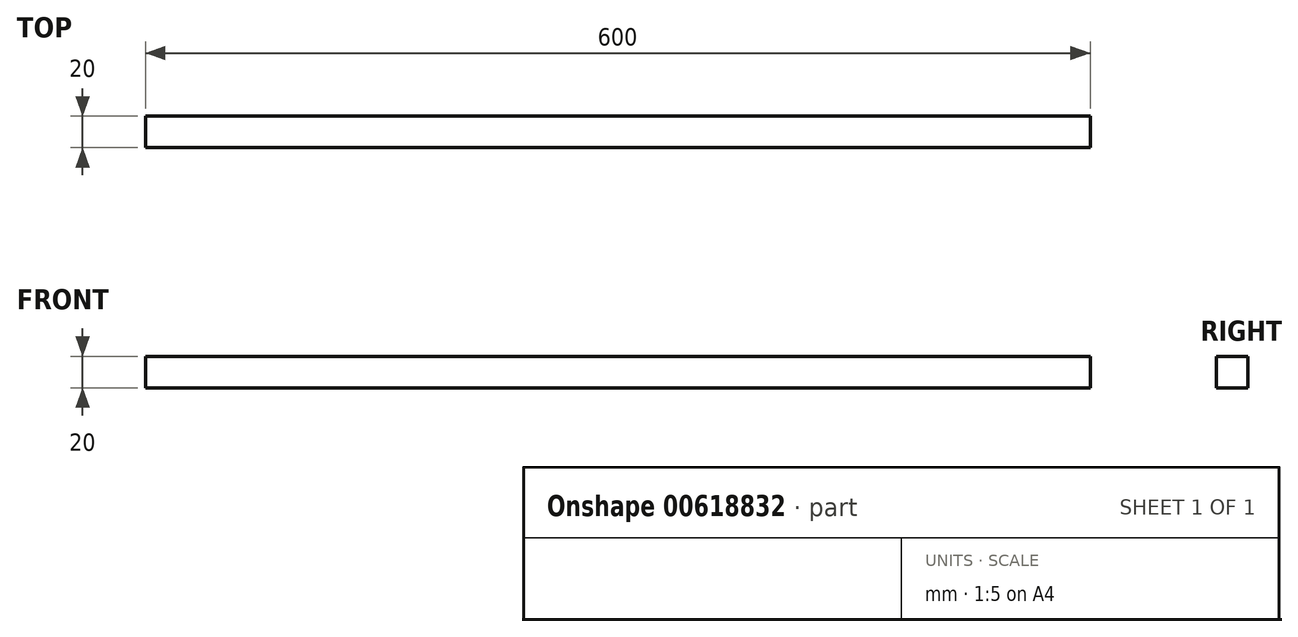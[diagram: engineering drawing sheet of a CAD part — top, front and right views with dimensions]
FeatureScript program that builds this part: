
annotation { "Feature Type Name" : "Feature", "Feature Type Description" : "" }
export const myFeature = defineFeature(function(context is Context, id is Id, definition is map)
    precondition{}
    {
        {
            var Q0;
            Q0=qCreatedBy(makeId("Top.planeOp"),FACE);
            var sketch = newSketch(context, id + "F0", { "sketchPlane" : qUnion([Q0])});
            skLineSegment(sketch, "E0.bottom", {"start": v(-300, 10) * mm, "end": v(300, 10) * mm});
            skLineSegment(sketch, "E0.top", {"start": v(-300, -10) * mm, "end": v(300, -10) * mm});
            skLineSegment(sketch, "E0.left", {"start": v(-300, 10) * mm, "end": v(-300, -10) * mm});
            skLineSegment(sketch, "E0.right", {"start": v(300, 10) * mm, "end": v(300, -10) * mm});
            skPoint(sketch, "E0.middle", {"position": v(0, 0) * mm});
            skSolve(sketch);
        }
        {
            var Q0;
            Q0 = qSketchRegion(id + "F0", true);
            extrude(context, id + "F1", {"entities" : qUnion([Q0]), "depth" : 20 * mm, "offsetDistance" : 25 * mm});
        }
    });
